# Revit family: DC_Rheem_PLM_Raypak_B2004HWT
name_source: partatom
category: Plumbing Fixtures
revit_build: Autodesk Revit 2017 (Build: 20160225_1515(x64)
units: mm (PartAtom-declared; Revit-internal decimal feet)

## family parameters
Cut with Voids When Loaded = No
Host = Face
Part Type = Normal
Room Calculation Point = No
Round Connector Dimension = Use Radius
Shared = No

## types (4) — shared parameters
BaseHeight_ANZRS = 75 mm
BaseWidth_ANZRS = 75 mm
BoxHeight_ANZRS = 1195 mm  [stored 3.9206 ft]
ColdWaterPipeDiameter_ANZRS = 80 mm  [stored 0.262467 ft]
ColdWaterPipeDisi_ANZRS = 567 mm
ColdWaterPipeRadius_ANZRS = 40 mm  [stored 0.131234 ft]
ConnHeight_ANZRS = 910 mm
EleBoxHeight_ANZRS = 380 mm  [stored 1.24672 ft]
EleBoxHeightfromBase_ANZRS = 450 mm
EleBoxWidth_ANZRS = 160 mm
GasPipeDist_ANZRS = 210 mm
GasPipeHeight_ANZRS = 600 mm
Height_ANZRS = 3165 mm  [stored 10.3839 ft]
HotWaterPipeDist_ANZRS = 235 mm
Length_ANZRS = 1550 mm
Manufacturer = Raypak
Materials_ANZRS = Raypak - Grey Powder Coated Steel
PRVDiameter_ANZRS = 20 mm  [stored 0.0656168 ft]
PRVDist_ANZRS = 400 mm
PRVRadius_ANZRS = 10 mm  [stored 0.0328084 ft]
TopBigDia_ANZRS = 1000 mm  [stored 3.28084 ft]
TopH1_ANZRS = 300 mm
TopH2_ANZRS = 750 mm  [stored 2.46063 ft]
TopSmallDia_ANZRS = 610 mm  [stored 2.00131 ft]
URL = http://www.rheem.com.au
Width_ANZRS = 1430 mm
zero-valued in all types: BaseDist_ANZRS, Default Elevation

## per-type parameters (varying)
| type | GasPipeDiameter_ANZRS | GasPipeRadius_ANZRS | HotWaterPipeDiameter_ANZRS | HotWaterPipeRadius_ANZRS | Model | Type Comments |
| Raypak - Gas Water Heater- Outdoor - 2004 MJ/h  Natural gas, modulating gas control | 50 mm  [stored 0.164042 ft] | 25 mm  [stored 0.082021 ft] | 80 mm  [stored 0.262467 ft] | 40 mm  [stored 0.131234 ft] | B2004NCM/HWT | Recovery 7654L/h @ 50°C rise |
| Raypak - Gas Water Heater- Outdoor - 2004 MJ/h  Natural gas, On/Off gas control | 50 mm  [stored 0.164042 ft] | 25 mm  [stored 0.082021 ft] | 80 mm  [stored 0.262467 ft] | 40 mm  [stored 0.131234 ft] | B2004NCO/HWT | Recovery 7654L/h @ 50°C rise |
| Raypak - Gas Water Heater- Outdoor - 2150 MJ/h  Propane gas, modulating gas control | 40 mm  [stored 0.131234 ft] | 20 mm  [stored 0.0656168 ft] | 90 mm | 45 mm | B2004PCM/HWT | Recovery 8190L/h @ 50°C rise |
| Raypak - Gas Water Heater- Outdoor - 2150 MJ/h  Propane gas, On/Off gas control | 40 mm  [stored 0.131234 ft] | 20 mm  [stored 0.0656168 ft] | 80 mm  [stored 0.262467 ft] | 40 mm  [stored 0.131234 ft] | B2004PCO/HWT | Recovery 8190L/h @ 50°C rise |

note: column(s) folded — value = type name in every type: Description

note: [stored X ft] marks values corroborated as IEEE doubles in the binary element streams (Revit-internal decimal feet)

## geometry (parser evidence)
native form markers: Blend x6, Sweep x2
no freeform markers — native parametric forms only
